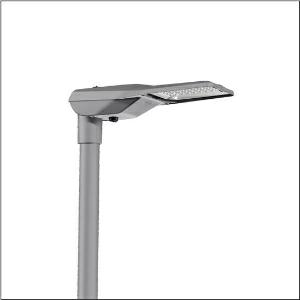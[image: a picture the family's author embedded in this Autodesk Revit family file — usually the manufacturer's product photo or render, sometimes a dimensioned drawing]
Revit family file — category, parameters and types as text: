
# Revit family: streetlight_sl_21_mini___st1_0a_5xe2d43t08gb_73de
name_source: partatom
category: Lighting Fixtures
units: mm (PartAtom-declared; Revit-internal decimal feet)

## family parameters
Cut with Voids When Loaded = No
Host = Face
Light Source = No
Part Type = Normal
Room Calculation Point = No
Round Connector Dimension = Use Diameter
Shared = No

## types (1)
- --- (1 x LED, 6180 lm, 40.4 W, 4000K)
    Apparent Load = 40 VA
    CIE Flux Codes = 37 72 97 100 100
    Color Rendering = 70
    Color Temperature = 4000K
    Default Elevation = 1800 mm
    Description = Streetlight SL 21 mini, mast luminaire, primary light control with lens, of PMMA, primary optical cover: cover, of toughened safety glass, transparent, light distribution: ST1.0a, light emission: direct distribution, primary light characteristic: asymmetric, installation type: side-entry, post-top, LED, High Power LED, rated luminous flux: 6.180lm, luminous efficacy: 153lm/W, light colour: 740, colour temperature: 4000K, control: overheat protection, constant luminous flux control, time-dependent luminous flux control, flexible luminous flux parameterisation, presetting dimming logarithmic, mains connection: 220..240V, AC, 50/60Hz, start of lifetime: 40W, end of service life: 41W, reduction: 19W, luminaire housing, of diecast aluminium, powder-coated, Siteco® metallic grey (DB 702S), corrosivity category C5 mid according to DIN EN ISO 12944, please order mast flange separately, inclination adjustable: 0°, 5°, 10°, 15°, sealing non-destructively replaceable, multi-level sealing system, length: 628mm, width: 235mm, height: 110mm, mast flange for spigot size: 42mm (side-entry): 5XC10008XM4, 60/48mm (side-entry/post-top): 5XC10108XM2, 76/60mm (side-entry/post-top): 5XC10108XM1, Smart Interface below and above, protection rating (complete): IP66, insulation class (complete): insulation class II (safety insulation), certification: CE, ENEC, ENEC+, VDE, impact resistance: IK09, permissible operating ambient temperature for outdoor applications: -40..+50°C, standard-compliant lighting for roads and squares, packaging unit: 1 piece

Light Distribution: ST1.0a
    Height = 110 mm
    Lamp = 1 x LED
    Lamp Light Flux = 6180 lm
    Lamp Power = 40.4 W
    Lamp count = 1
    Length = 625 mm
    Luminous efficacy = 153 lm/W
    Manufacturer = Siteco
    ModVariant = No
    Model = 5XE2D43T08GB
    Number of Poles = 1
    OnlyDefault = Yes
    Power Factor = 1
    Product Name = Streetlight SL 21 mini | ST1.0a
    Product group = mast luminaire | pylon top
    ProductGroupID = 6100
    Protection Class = Protection class II
    Protection Degree = IP 66
    RLX_Detail_Level = 1
    RLX_Emergency_Light_Flux = 0 lm
    RLX_Emergency_Type = 0
    RLX_Emergency_Type_DB = No
    RlxData = <blob elided: 92385 chars, md5=f8438841>
    Socket = socket
    Standby Power = 0 W
    System Light Flux = 6180 lm
    System Power = 40 W
    Type Comments = factory setting: luminous flux: 100 % | dim-lin: 254 | 812 mA
    Type Image = l_1003514.jpg
    URL = http://relux.com
    VarID = @adj_122269
    Voltage = 0 V
    Weight = 0.00 kg
    Width = 234 mm

## geometry (parser evidence)
native form markers: Blend x4, Sweep x13
no freeform markers — native parametric forms only
